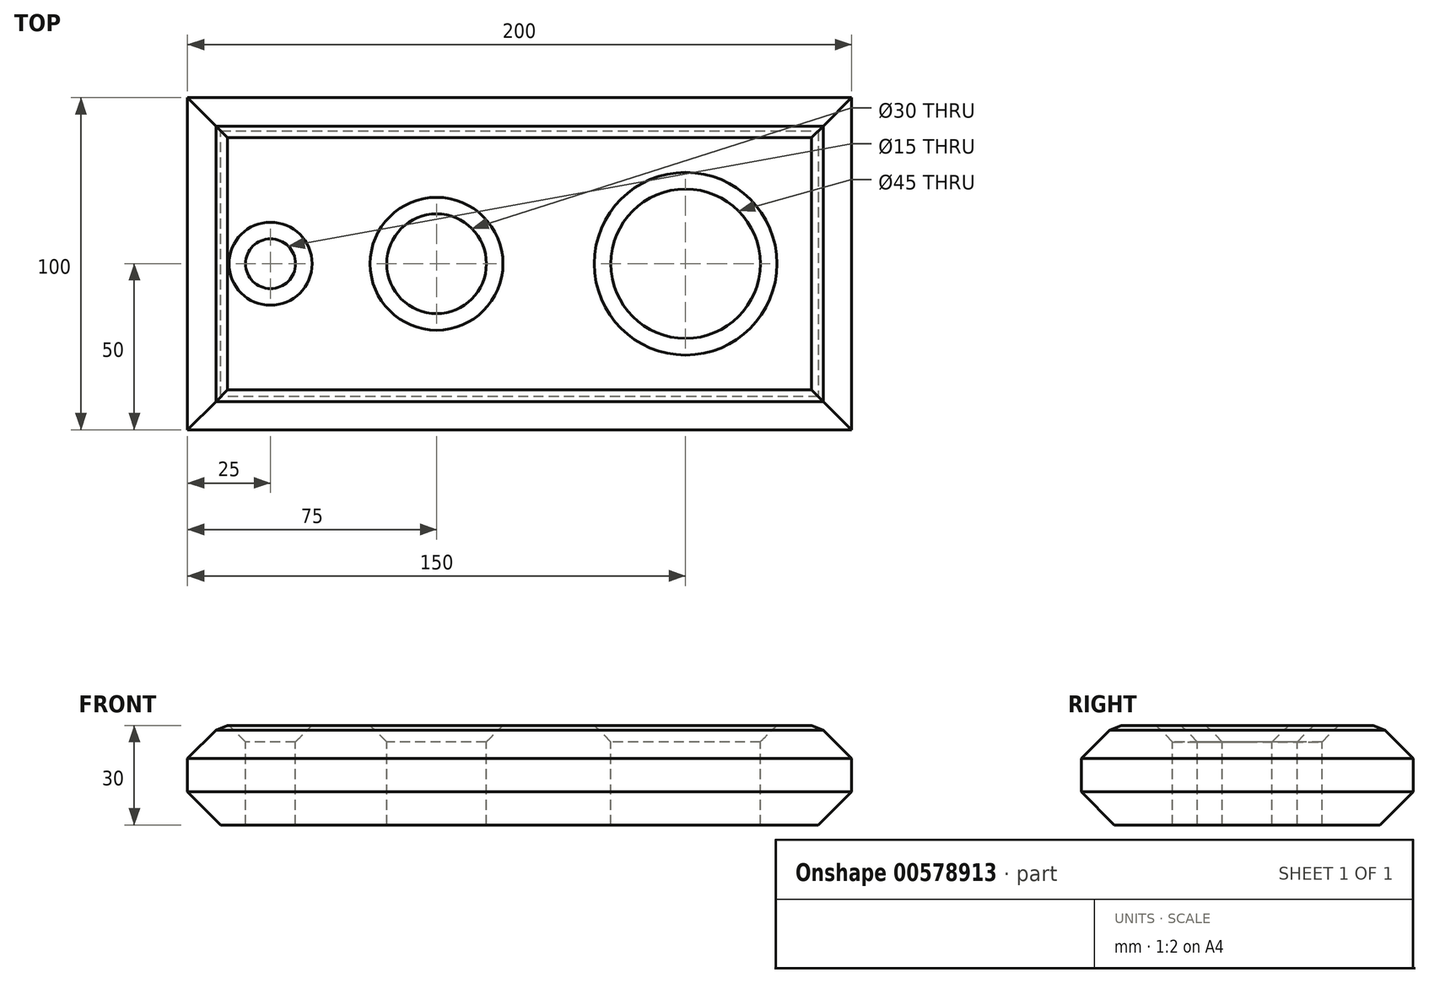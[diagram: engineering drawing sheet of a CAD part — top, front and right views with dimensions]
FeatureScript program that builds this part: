
annotation { "Feature Type Name" : "Feature", "Feature Type Description" : "" }
export const myFeature = defineFeature(function(context is Context, id is Id, definition is map)
    precondition{}
    {
        {
            var Q0;
            Q0=qCreatedBy(makeId("Top.planeOp"),FACE);
            var sketch = newSketch(context, id + "F0", { "sketchPlane" : qUnion([Q0])});
            skLineSegment(sketch, "E0.bottom", {"start": v(100, 50) * mm, "end": v(-100, 50) * mm});
            skLineSegment(sketch, "E0.top", {"start": v(100, -50) * mm, "end": v(-100, -50) * mm});
            skLineSegment(sketch, "E0.left", {"start": v(100, 50) * mm, "end": v(100, -50) * mm});
            skLineSegment(sketch, "E0.right", {"start": v(-100, 50) * mm, "end": v(-100, -50) * mm});
            skPoint(sketch, "E0.middle", {"position": v(0, 0) * mm});
            skSolve(sketch);
        }
        {
            var Q0;
            Q0 = qSketchRegion(id + "F0", true);
            extrude(context, id + "F1", {"entities" : qUnion([Q0]), "endBound" : BoundingType.SYMMETRIC, "depth" : 30 * mm, "offsetDistance" : 25 * mm});
        }
        {
            var Q0;
            Q0=makeQuery(id+"F1.opExtrude","CAP_FACE",FACE,{"disambiguationData":[OSD([sQuery(id+"F0.wireOp",EDGE,"E0.bottom"),sQuery(id+"F0.wireOp",EDGE,"E0.top"),sQuery(id+"F0.wireOp",EDGE,"E0.left"),sQuery(id+"F0.wireOp",EDGE,"E0.right")])],"isStart":false});
            var Q1;
            Q1=makeQuery(id+"F1.opExtrude","CAP_FACE",FACE,{"disambiguationData":[OSD([sQuery(id+"F0.wireOp",EDGE,"E0.bottom"),sQuery(id+"F0.wireOp",EDGE,"E0.top"),sQuery(id+"F0.wireOp",EDGE,"E0.left"),sQuery(id+"F0.wireOp",EDGE,"E0.right")])],"isStart":true});
            chamfer(context, id + "F2", {"entities" : qUnion([Q0, Q1]), "width" : 10 * mm, "tangentPropagation" : true});
        }
        {
            var Q0;
            Q0=makeQuery(id+"F1.opExtrude","CAP_FACE",FACE,{"disambiguationData":[OSD([sQuery(id+"F0.wireOp",EDGE,"E0.bottom"),sQuery(id+"F0.wireOp",EDGE,"E0.top"),sQuery(id+"F0.wireOp",EDGE,"E0.left"),sQuery(id+"F0.wireOp",EDGE,"E0.right")])],"isStart":false});
            var sketch = newSketch(context, id + "F3", { "sketchPlane" : qUnion([Q0])});
            skCircle(sketch, "E1", {"center": v(-75, 0) * mm, "radius": 7.5 * mm});
            skCircle(sketch, "E2", {"center": v(-25, 0) * mm, "radius": 15 * mm});
            skCircle(sketch, "E3", {"center": v(50, 0) * mm, "radius": 22.5 * mm});
            skSolve(sketch);
        }
        {
            var Q0;
            Q0=makeQuery(id+"F3.imprint","IMPRINT",FACE,{"disambiguationData":[TD([[makeQuery(id+"F3.imprint","IMPRINT",EDGE,{"derivedFrom":sQuery(id+"F3.wireOp",EDGE,"E2")}),1.0]])]});
            var Q1;
            Q1=makeQuery(id+"F3.imprint","IMPRINT",FACE,{"disambiguationData":[TD([[makeQuery(id+"F3.imprint","IMPRINT",EDGE,{"derivedFrom":sQuery(id+"F3.wireOp",EDGE,"E1")}),1.0]])]});
            var Q2;
            Q2=makeQuery(id+"F3.imprint","IMPRINT",FACE,{"disambiguationData":[TD([[makeQuery(id+"F3.imprint","IMPRINT",EDGE,{"derivedFrom":sQuery(id+"F3.wireOp",EDGE,"E3")}),1.0]])]});
            extrude(context, id + "F4", {"entities" : qUnion([Q0, Q1, Q2]), "operationType" : NewBodyOperationType.REMOVE, "endBound" : BoundingType.THROUGH_ALL, "oppositeDirection" : true, "depth" : 25 * mm, "offsetDistance" : 25 * mm});
        }
        {
            var Q0;
            Q0=makeQuery(id+"F4.boolean.opBoolean","COPY",EDGE,{"derivedFrom":makeQuery(id+"F4.opExtrude","CAP_EDGE",EDGE,{"disambiguationData":[OSD([sQuery(id+"F3.wireOp",EDGE,"E3")])],"isStart":true})});
            var Q1;
            Q1=makeQuery(id+"F4.boolean.opBoolean","COPY",EDGE,{"derivedFrom":makeQuery(id+"F4.opExtrude","CAP_EDGE",EDGE,{"disambiguationData":[OSD([sQuery(id+"F3.wireOp",EDGE,"E2")])],"isStart":true})});
            var Q2;
            Q2=makeQuery(id+"F1.opExtrude","CAP_FACE",FACE,{"disambiguationData":[OSD([sQuery(id+"F0.wireOp",EDGE,"E0.bottom"),sQuery(id+"F0.wireOp",EDGE,"E0.top"),sQuery(id+"F0.wireOp",EDGE,"E0.left"),sQuery(id+"F0.wireOp",EDGE,"E0.right")])],"isStart":false});
            chamfer(context, id + "F5", {"entities" : qUnion([Q0, Q1, Q2]), "width" : 5 * mm, "tangentPropagation" : true});
        }
    });
